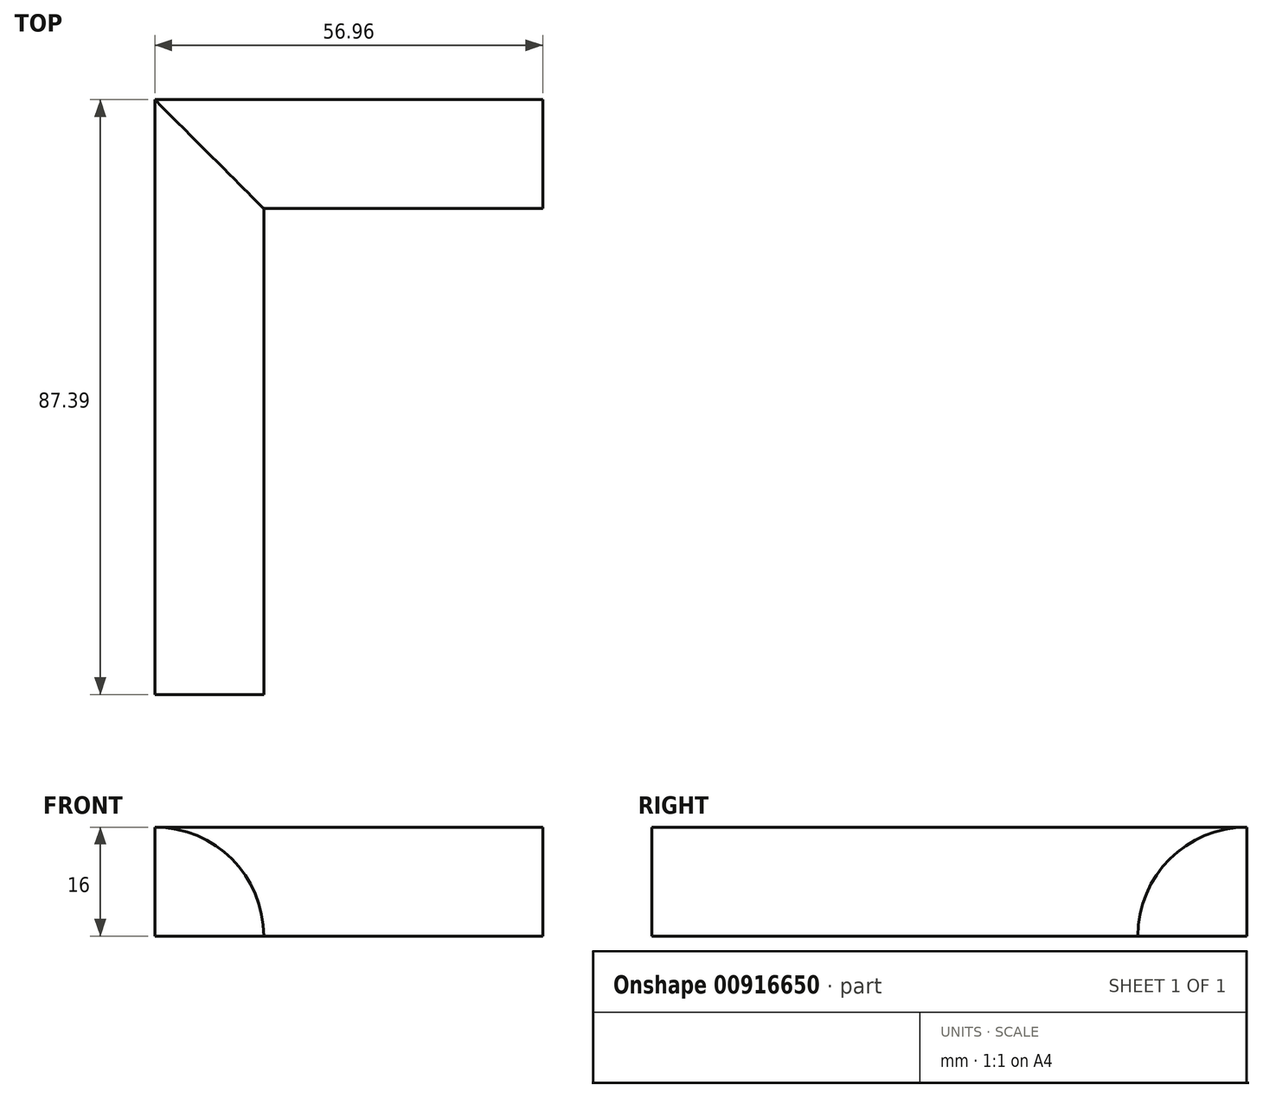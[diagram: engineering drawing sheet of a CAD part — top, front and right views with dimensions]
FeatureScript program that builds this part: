
annotation { "Feature Type Name" : "Feature", "Feature Type Description" : "" }
export const myFeature = defineFeature(function(context is Context, id is Id, definition is map)
    precondition{}
    {
        {
            var Q0;
            Q0=qCreatedBy(makeId("Front.planeOp"),FACE);
            var sketch = newSketch(context, id + "F0", { "sketchPlane" : qUnion([Q0])});
            skLineSegment(sketch, "E0", {"start": v(0, 16) * mm, "end": v(0, 0) * mm});
            skLineSegment(sketch, "E1", {"start": v(0, 0) * mm, "end": v(16, 0) * mm});
            skArc(sketch, "E2", {"start": v(16, 0) * mm, "mid": v(11.31, 11.31) * mm, "end": v(0, 16) * mm});
            skSolve(sketch);
        }
        {
            var Q0;
            Q0 = qSketchRegion(id + "F0", true);
            extrude(context, id + "F1", {"entities" : qUnion([Q0]), "depth" : 87.4 * mm, "offsetDistance" : 25 * mm});
        }
        {
            var Q0;
            Q0=qCreatedBy(makeId("Right.planeOp"),FACE);
            var sketch = newSketch(context, id + "F2", { "sketchPlane" : qUnion([Q0])});
            skLineSegment(sketch, "E3", {"start": v(0, 0) * mm, "end": v(0, 16) * mm});
            skLineSegment(sketch, "E4", {"start": v(0, 0) * mm, "end": v(-16, 0) * mm});
            skArc(sketch, "E5", {"start": v(-16, 0) * mm, "mid": v(-11.31, 11.31) * mm, "end": v(0, 16) * mm});
            skSolve(sketch);
        }
        {
            var Q0;
            Q0 = qSketchRegion(id + "F2", true);
            extrude(context, id + "F3", {"entities" : qUnion([Q0]), "operationType" : NewBodyOperationType.ADD, "depth" : 56.96 * mm, "offsetDistance" : 25 * mm});
        }
    });
